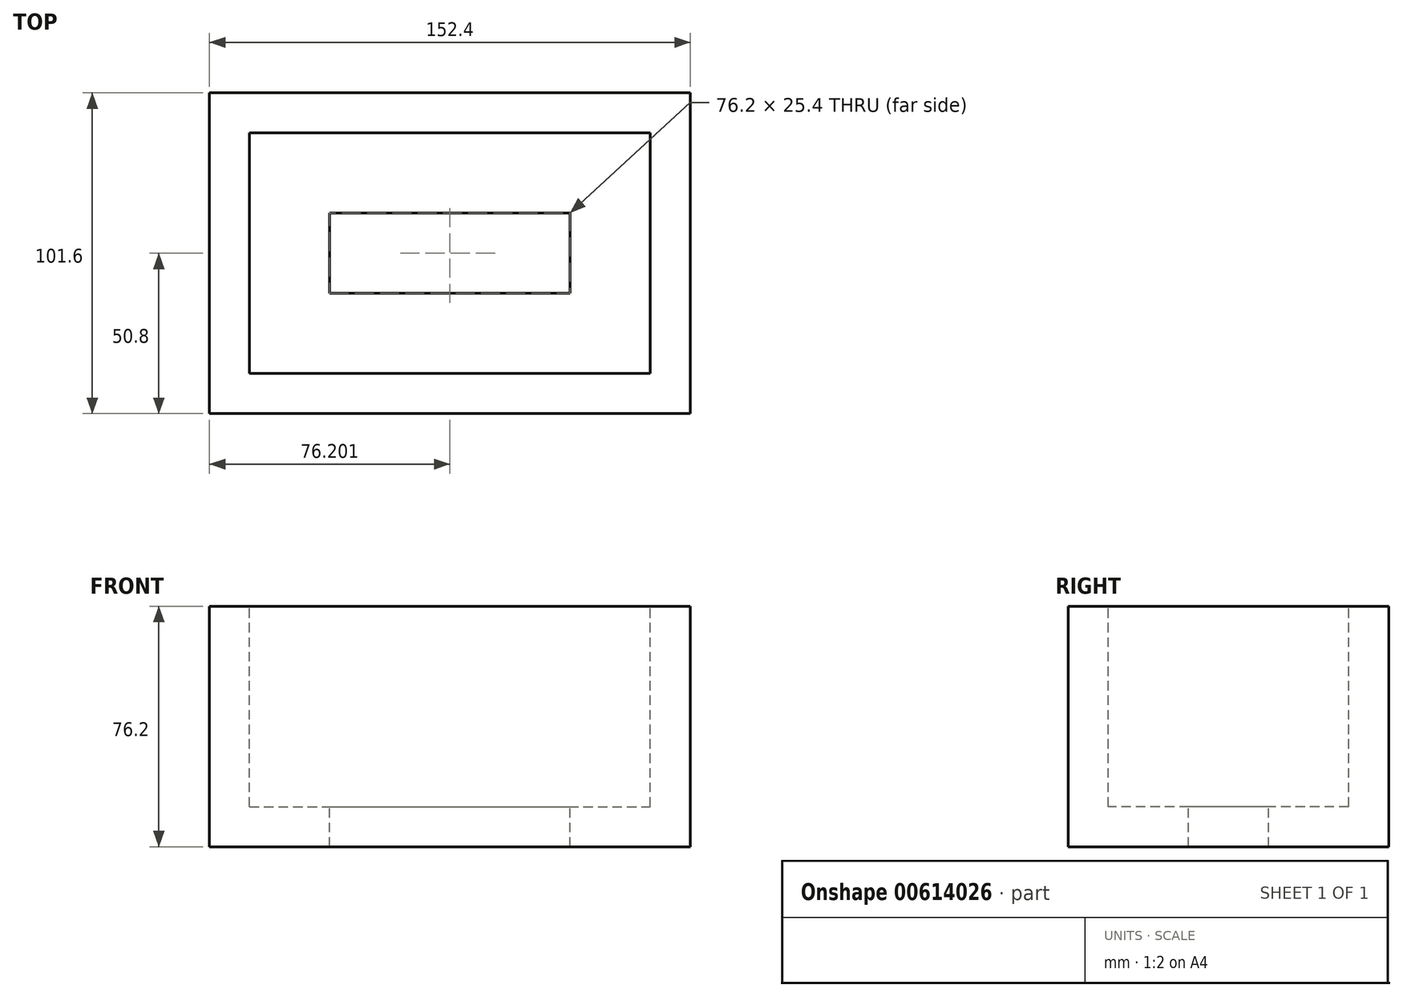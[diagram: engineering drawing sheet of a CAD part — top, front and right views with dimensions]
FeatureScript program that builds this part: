
annotation { "Feature Type Name" : "Feature", "Feature Type Description" : "" }
export const myFeature = defineFeature(function(context is Context, id is Id, definition is map)
    precondition{}
    {
        {
            var Q0;
            Q0=qCreatedBy(makeId("Front.planeOp"),FACE);
            var sketch = newSketch(context, id + "F0", { "sketchPlane" : qUnion([Q0])});
            skLineSegment(sketch, "E0", {"start": v(44.83, 27.56) * mm, "end": v(44.83, -48.64) * mm});
            skLineSegment(sketch, "E1", {"start": v(44.83, -48.64) * mm, "end": v(197.23, -48.64) * mm});
            skLineSegment(sketch, "E2", {"start": v(197.23, -48.64) * mm, "end": v(197.23, 27.56) * mm});
            skLineSegment(sketch, "E3", {"start": v(197.23, 27.56) * mm, "end": v(44.83, 27.56) * mm});
            skSolve(sketch);
        }
        {
            var Q0;
            Q0=makeQuery(id+"F0.imprint","IMPRINT",FACE,{"disambiguationData":[TD([[makeQuery(id+"F0.imprint","IMPRINT",EDGE,{"derivedFrom":sQuery(id+"F0.wireOp",EDGE,"E0")}),1.0]])]});
            extrude(context, id + "F1", {"entities" : qUnion([Q0]), "depth" : 101.6 * mm, "offsetDistance" : 25.4 * mm});
        }
        {
            var Q0;
            Q0=makeQuery(id+"F1.opExtrude","SWEPT_FACE",FACE,{"disambiguationData":[OSD([sQuery(id+"F0.wireOp",EDGE,"E3")])]});
            var sketch = newSketch(context, id + "F2", { "sketchPlane" : qUnion([Q0])});
            skLineSegment(sketch, "E4.bottom", {"start": v(57.53, -12.7) * mm, "end": v(184.53, -12.7) * mm});
            skLineSegment(sketch, "E4.top", {"start": v(57.53, -88.9) * mm, "end": v(184.53, -88.9) * mm});
            skLineSegment(sketch, "E4.left", {"start": v(57.53, -12.7) * mm, "end": v(57.53, -88.9) * mm});
            skLineSegment(sketch, "E4.right", {"start": v(184.53, -12.7) * mm, "end": v(184.53, -88.9) * mm});
            skSolve(sketch);
        }
        {
            var Q0;
            Q0=makeQuery(id+"F2.imprint","IMPRINT",FACE,{"disambiguationData":[TD([[makeQuery(id+"F2.imprint","IMPRINT",EDGE,{"derivedFrom":sQuery(id+"F2.wireOp",EDGE,"E4.bottom")}),-1.0]])]});
            extrude(context, id + "F3", {"entities" : qUnion([Q0]), "operationType" : NewBodyOperationType.REMOVE, "oppositeDirection" : true, "depth" : 63.5 * mm, "offsetDistance" : 25.4 * mm});
        }
        {
            var Q0;
            Q0=makeQuery(id+"F3.boolean.opBoolean","COPY",FACE,{"derivedFrom":makeQuery(id+"F3.opExtrude","CAP_FACE",FACE,{"disambiguationData":[OSD([sQuery(id+"F2.wireOp",EDGE,"E4.bottom"),sQuery(id+"F2.wireOp",EDGE,"E4.top"),sQuery(id+"F2.wireOp",EDGE,"E4.left"),sQuery(id+"F2.wireOp",EDGE,"E4.right")])],"isStart":false})});
            var sketch = newSketch(context, id + "F4", { "sketchPlane" : qUnion([Q0])});
            skLineSegment(sketch, "E5.bottom", {"start": v(82.93, -38.1) * mm, "end": v(159.13, -38.1) * mm});
            skLineSegment(sketch, "E5.top", {"start": v(82.93, -63.5) * mm, "end": v(159.13, -63.5) * mm});
            skLineSegment(sketch, "E5.left", {"start": v(82.93, -38.1) * mm, "end": v(82.93, -63.5) * mm});
            skLineSegment(sketch, "E5.right", {"start": v(159.13, -38.1) * mm, "end": v(159.13, -63.5) * mm});
            skSolve(sketch);
        }
        {
            var Q0;
            Q0=makeQuery(id+"F4.imprint","IMPRINT",FACE,{"disambiguationData":[TD([[makeQuery(id+"F4.imprint","IMPRINT",EDGE,{"derivedFrom":sQuery(id+"F4.wireOp",EDGE,"E5.bottom")}),-1.0]])]});
            extrude(context, id + "F5", {"entities" : qUnion([Q0]), "operationType" : NewBodyOperationType.REMOVE, "oppositeDirection" : true, "depth" : 12.7 * mm, "offsetDistance" : 25.4 * mm});
        }
    });
